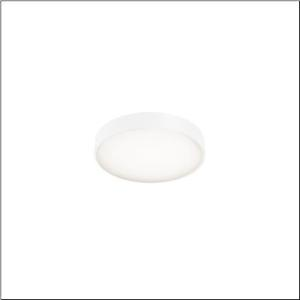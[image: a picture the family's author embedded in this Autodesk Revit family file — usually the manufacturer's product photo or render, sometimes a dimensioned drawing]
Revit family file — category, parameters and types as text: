
# Revit family: round_21_s_51mr34fd0321w
name_source: partatom
category: Lighting Fixtures
units: mm (PartAtom-declared; Revit-internal decimal feet)

## family parameters
Cut with Voids When Loaded = No
Host = Face
Light Source = No
Part Type = Normal
Room Calculation Point = No
Round Connector Dimension = Use Diameter
Shared = No

## types (1)
- Round 21 S (1 x LED, 3750 lm, 30.3 W, 3000K)
    Apparent Load = 30 VA
    CIE Flux Codes = 49 80 96 100 100
    Color Rendering = 80
    Color Temperature = 3000K
    Default Elevation = 1800 mm
    Description = Round 21 S, wall and ceiling luminaire, primary optical cover: cover, of PMMA, opal, light emission: direct distribution, primary light characteristic: symmetric, installation type: suspended mounting, surface-mounted, LED, rated luminous flux: 3.750lm, luminous efficacy: 124lm/W, light colour: 830, colour temperature: 3000K, control gear: DALI 2, with terminal, 5-pole, mains connection: 230V, AC, 50/60Hz, rated input power: 30.3W, housing, of aluminium, coated, white, diameter: 400mm, height: 62mm, protection rating (complete): IP40, insulation class (complete): insulation class I (protective earthing), certification: CE, impact resistance: IK04, permissible operating ambient temperature: -10..+35°C, packaging unit: 1 piece
    Height = 87 mm
    Lamp = 1 x LED
    Lamp Light Flux = 3750 lm
    Lamp Power = 30.3 W
    Lamp count = 1
    Length = 400 mm
    Luminous efficacy = 124 lm/W
    Manufacturer = Siteco
    ModVariant = No
    Model = 51MR34FD0321W
    Mounting Place = Wall
    Mounting Type = Surface mounted
    Number of Poles = 1
    OnlyDefault = Yes
    Power Factor = 1
    Product Name = Round 21 S
    Product group = wall and ceiling luminaire
    ProductGroupID = 2001
    Protection Class = Protection class I
    Protection Degree = IP 40
    RLX_Detail_Level = 1
    RLX_Emergency_Light_Flux = 0 lm
    RLX_Emergency_Type = 0
    RLX_Emergency_Type_DB = No
    RlxData = <blob elided: 9517 chars, md5=c317c139>
    Socket = socket
    Standby Power = 0 W
    System Light Flux = 3750 lm
    System Power = 30 W
    Type Comments = Product without accessories
    Type Image = l_1258307.jpg
    URL = http://relux.com
    VarID = ---
    Voltage = 0 V
    Weight = 0.00 kg
    Width = 0 mm  [stored 0 ft]

note: [stored X ft] marks values corroborated as IEEE doubles in the binary element streams (Revit-internal decimal feet)

## geometry (parser evidence)
native form markers: Sweep x8
no freeform markers — native parametric forms only
